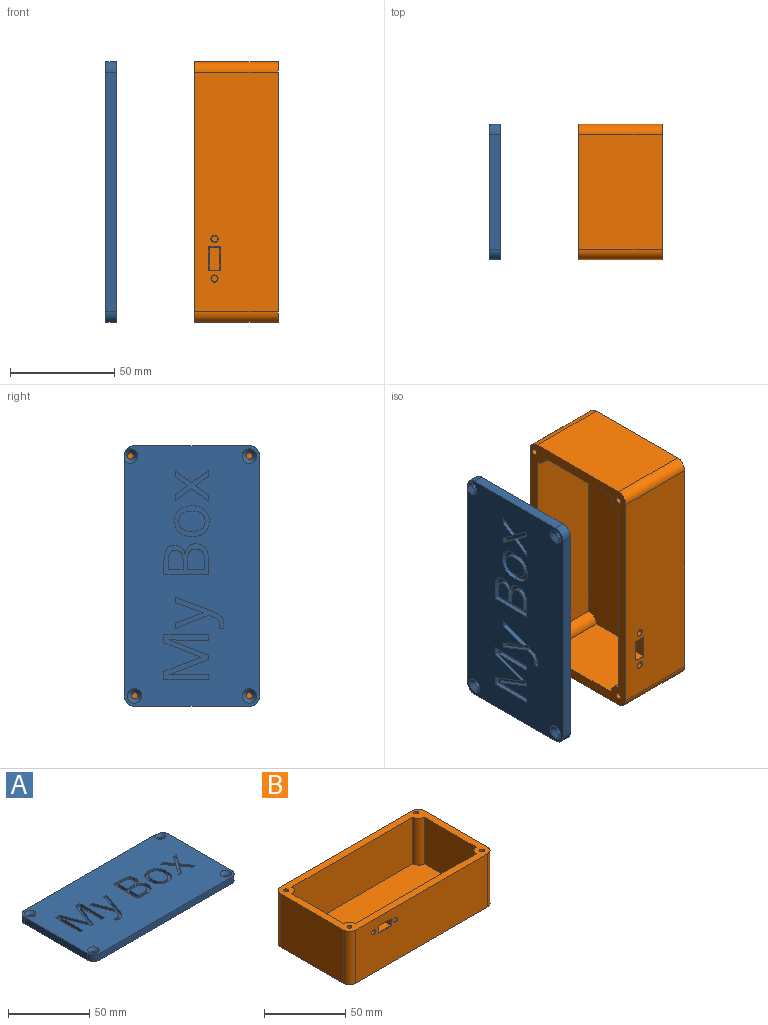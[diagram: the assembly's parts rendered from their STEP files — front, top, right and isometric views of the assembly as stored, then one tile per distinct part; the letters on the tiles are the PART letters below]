
ASSEMBLY  parts=2 mates=1
PART A: 114 faces, bbox 125.4x65.9x5.4 mm
  f0: plane 125x65mm, normal (0,0,1), area 7082mm2, adj f1,f2,f3,f4,f5,f6,f7,f12
  f1: plane 55x5mm, normal (1,0,0), area 275mm2, adj f0,f2,f12,f13
  f2: cylinder r=5mm len=5mm, axis (0,0,-1), area 38.5mm2, adj f0,f1,f3,f13,f112
  f3: plane 115.36x5.36mm, normal (0,1,0), area 574.4mm2, adj f0,f2,f4,f13,f112
  f4: cylinder r=5mm len=5mm, axis (0,0,-1), area 39.3mm2, adj f0,f3,f5,f13
  f5: plane 55x5mm, normal (-1,0,0), area 275mm2, adj f0,f4,f6,f13
  f6: cylinder r=5mm len=5mm, axis (0,0,-1), area 39.3mm2, adj f0,f5,f7,f13
  f7: plane 115x5mm, normal (0,-1,0), area 575mm2, adj f0,f6,f12,f13
  f8: cylinder r=1.5mm len=3mm, axis (0,0,-1), area 28.3mm2, adj f13,f110
  f9: cylinder r=1.5mm len=3mm, axis (0,0,-1), area 28.3mm2, adj f13,f112
  f10: cylinder r=1.5mm len=3mm, axis (0,0,-1), area 28.3mm2, adj f13,f113
  f11: cylinder r=1.5mm len=3mm, axis (0,0,-1), area 28.3mm2, adj f13,f111
  f12: cylinder r=5mm len=5mm, axis (0,0,-1), area 39.3mm2, adj f0,f1,f7,f13
  f13: plane 125x65mm, normal (0,0,-1), area 8075.3mm2, adj f1,f2,f3,f4,f5,f6,f7,f8
  f14: plane 2.62x2mm, normal (0,-1,0), area 5.2mm2, adj f0,f15,f29,f30
  f15: plane 16.2x6.5mm, normal (0.93,0.37,0), area 34.9mm2, adj f0,f14,f16,f30
  f16: plane 2.29x2mm, normal (0.93,-0.37,0), area 4.9mm2, adj f0,f15,f17,f30
  f17: extruded ~3.59x2.82mm, area 9.8mm2, adj f0,f16,f18,f30
  f18: extruded ~2x1.81mm, area 3.6mm2, adj f0,f17,f19,f30
  f19: plane 2x1.95mm, normal (1,0,0), area 3.9mm2, adj f0,f18,f20,f30
  f20: extruded ~2.21x2mm, area 4.5mm2, adj f0,f19,f21,f30
  f21: extruded ~3.37x2mm, area 7.3mm2, adj f0,f20,f22,f30
  f22: extruded ~3.86x2.4mm, area 9.2mm2, adj f0,f21,f23,f30
  f23: plane 18.35x6.93mm, normal (-0.94,0.35,0), area 39.2mm2, adj f0,f22,f24,f30
  f24: plane 2.62x2mm, normal (0,-1,0), area 5.2mm2, adj f0,f23,f25,f30
  f25: extruded ~11.16x3.99mm, area 23.7mm2, adj f0,f24,f26,f30
  f26: extruded ~2.57x2mm, area 5.4mm2, adj f0,f25,f27,f30
  f27: plane 2x0.12mm, normal (0,-1,0), area 0.2mm2, adj f0,f26,f28,f30
  f28: extruded ~4.54x2mm, area 9.5mm2, adj f0,f27,f29,f30
  f29: plane 9.19x3.53mm, normal (-0.93,-0.36,0), area 19.7mm2, adj f0,f14,f28,f30
  f30: plane 23.35x15.12mm, normal (0,0,1), area 100.8mm2, adj f14,f15,f16,f17,f18,f19,f20,f21
  f31: plane 7.87x5.6mm, normal (0.81,0.58,0), area 19.3mm2, adj f0,f32,f42,f43
  f32: plane 8.25x5.89mm, normal (0.81,-0.58,0), area 20.3mm2, adj f0,f31,f33,f43
  f33: plane 2.76x2mm, normal (0,1,0), area 5.5mm2, adj f0,f32,f34,f43
  f34: plane 6.53x4.56mm, normal (-0.82,0.57,0), area 15.9mm2, adj f0,f33,f35,f43
  f35: plane 6.53x4.52mm, normal (0.82,0.57,0), area 15.9mm2, adj f0,f34,f36,f43
  f36: plane 2.76x2mm, normal (0,1,0), area 5.5mm2, adj f0,f35,f37,f43
  f37: plane 8.25x5.89mm, normal (-0.81,-0.58,0), area 20.3mm2, adj f0,f36,f38,f43
  f38: plane 7.87x5.6mm, normal (-0.81,0.58,0), area 19.3mm2, adj f0,f37,f39,f43
  f39: plane 2.75x2mm, normal (0,-1,0), area 5.5mm2, adj f0,f38,f40,f43
  f40: plane 6.17x4.23mm, normal (0.82,-0.57,0), area 15mm2, adj f0,f39,f41,f43
  f41: plane 6.17x4.25mm, normal (-0.82,-0.57,0), area 15mm2, adj f0,f40,f42,f43
  f42: plane 2.78x2mm, normal (0,-1,0), area 5.6mm2, adj f0,f31,f41,f43
  f43: plane 16.11x14.6mm, normal (0,0,1), area 82.1mm2, adj f31,f32,f33,f34,f35,f36,f37,f38
  f44: extruded ~4.71x2mm, area 9.9mm2, adj f45,f60,f61,f108
  f45: extruded ~4.69x2mm, area 9.9mm2, adj f44,f46,f61,f108
  f46: extruded ~3.62x2mm, area 8.2mm2, adj f45,f47,f61,f108
  f47: extruded ~3.67x2mm, area 8.3mm2, adj f46,f48,f61,f108
  f48: extruded ~4.67x2mm, area 9.8mm2, adj f47,f49,f61,f108
  f49: extruded ~4.71x2mm, area 9.9mm2, adj f48,f50,f61,f108
  f50: extruded ~3.64x2mm, area 8.3mm2, adj f49,f60,f61,f108
  f51: extruded ~6.16x2mm, area 13.2mm2, adj f0,f52,f59,f61
  f52: extruded ~6.09x2mm, area 13.1mm2, adj f0,f51,f53,f61
  f53: extruded ~5.37x2.25mm, area 12mm2, adj f0,f52,f54,f61
  f54: extruded ~5.47x2.2mm, area 12.2mm2, adj f0,f53,f55,f61
  f55: extruded ~6.14x2mm, area 13.2mm2, adj f0,f54,f56,f61
  f56: extruded ~4.44x2mm, area 9.1mm2, adj f0,f55,f57,f61
  f57: extruded ~2.91x2.59mm, area 7.9mm2, adj f0,f56,f58,f61
  f58: extruded ~3.84x2mm, area 8mm2, adj f0,f57,f59,f61
  f59: extruded ~5.48x2.21mm, area 12.2mm2, adj f0,f51,f58,f61
  f60: extruded ~3.63x2mm, area 8.3mm2, adj f44,f50,f61,f108
  f61: plane 16.71x14.81mm, normal (0,0,1), area 99.7mm2, adj f44,f45,f46,f47,f48,f49,f50,f51
  f62: plane 8.04x2mm, normal (-1,0,0), area 16.1mm2, adj f63,f86,f87,f109
  f63: plane 4.28x2mm, normal (0,1,0), area 8.6mm2, adj f62,f64,f87,f109
  f64: extruded ~4.09x2mm, area 8.5mm2, adj f63,f65,f87,f109
  f65: extruded ~2.94x2mm, area 6.7mm2, adj f64,f66,f87,f109
  f66: extruded ~3.16x2mm, area 7.1mm2, adj f65,f67,f87,f109
  f67: extruded ~3.92x2mm, area 8.2mm2, adj f66,f86,f87,f109
  f68: plane 4.12x2mm, normal (0,-1,0), area 8.2mm2, adj f69,f84,f87,f88
  f69: plane 7.04x2mm, normal (-1,0,0), area 14.1mm2, adj f68,f70,f87,f88
  f70: plane 3.68x2mm, normal (0,1,0), area 7.4mm2, adj f69,f71,f87,f88
  f71: extruded ~4.12x2mm, area 8.5mm2, adj f70,f72,f87,f88
  f72: extruded ~2.61x2mm, area 6.1mm2, adj f71,f73,f87,f88
  f73: extruded ~2.8x2mm, area 6.3mm2, adj f72,f84,f87,f88
  f74: plane 6.07x2mm, normal (0,-1,0), area 12.1mm2, adj f0,f75,f85,f87
  f75: plane 21.5x2mm, normal (1,0,0), area 43mm2, adj f0,f74,f76,f87
  f76: plane 7.5x2mm, normal (0,1,0), area 15mm2, adj f0,f75,f77,f87
  f77: extruded ~5.45x2mm, area 11.6mm2, adj f0,f76,f78,f87
  f78: extruded ~4.5x2mm, area 10.1mm2, adj f0,f77,f79,f87
  f79: extruded ~5.15x4.9mm, area 15.7mm2, adj f0,f78,f80,f87
  f80: plane 2x0.15mm, normal (-1,0,0), area 0.3mm2, adj f0,f79,f81,f87
  f81: extruded ~3.11x2mm, area 7.1mm2, adj f0,f80,f82,f87
  f82: extruded ~3.16x2mm, area 6.8mm2, adj f0,f81,f83,f87
  f83: extruded ~4.04x2mm, area 9.3mm2, adj f0,f82,f85,f87
  f84: extruded ~3.81x2mm, area 7.9mm2, adj f68,f73,f87,f88
  f85: extruded ~6.19x2mm, area 12.8mm2, adj f0,f74,f83,f87
  f86: plane 4.49x2mm, normal (0,-1,0), area 9mm2, adj f62,f67,f87,f109
  f87: plane 21.5x14.89mm, normal (0,0,1), area 157.6mm2, adj f62,f63,f64,f65,f66,f67,f68,f69
  f88: plane 9.09x7.04mm, normal (0,0,1), area 58.5mm2, adj f68,f69,f70,f71,f72,f73,f84
  f89: plane 19.05x7.29mm, normal (0.93,0.36,0), area 40.8mm2, adj f0,f90,f106,f107
  f90: plane 2.01x2mm, normal (0,1,0), area 4mm2, adj f0,f89,f91,f107
  f91: plane 19.03x7.35mm, normal (-0.93,0.36,0), area 40.8mm2, adj f0,f90,f92,f107
  f92: plane 2x0.12mm, normal (0,1,0), area 0.2mm2, adj f0,f91,f93,f107
  f93: extruded ~5.18x2mm, area 10.4mm2, adj f0,f92,f94,f107
  f94: plane 13.85x2mm, normal (1,0,0), area 27.7mm2, adj f0,f93,f95,f107
  f95: plane 2.5x2mm, normal (0,1,0), area 5mm2, adj f0,f94,f96,f107
  f96: plane 21.5x2mm, normal (-1,0,0), area 43mm2, adj f0,f95,f97,f107
  f97: plane 3.74x2mm, normal (0,-1,0), area 7.5mm2, adj f0,f96,f98,f107
  f98: plane 17.73x6.86mm, normal (0.93,-0.36,0), area 38mm2, adj f0,f97,f99,f107
  f99: plane 2x0.12mm, normal (0,-1,0), area 0.2mm2, adj f0,f98,f100,f107
  f100: plane 17.73x6.81mm, normal (-0.93,-0.36,0), area 38mm2, adj f0,f99,f101,f107
  f101: plane 3.76x2mm, normal (0,-1,0), area 7.5mm2, adj f0,f100,f102,f107
  f102: plane 21.5x2mm, normal (1,0,0), area 43mm2, adj f0,f101,f103,f107
  f103: plane 2.31x2mm, normal (0,1,0), area 4.6mm2, adj f0,f102,f104,f107
  f104: plane 13.67x2mm, normal (-1,0,0), area 27.3mm2, adj f0,f103,f105,f107
  f105: extruded ~5.38x2mm, area 10.8mm2, adj f0,f104,f106,f107
  f106: plane 2x0.12mm, normal (0,1,0), area 0.2mm2, adj f0,f89,f105,f107
  f107: plane 21.5x21.29mm, normal (0,0,1), area 197.6mm2, adj f89,f90,f91,f92,f93,f94,f95,f96
  f108: plane 12.58x9.75mm, normal (0,0,1), area 101.8mm2, adj f44,f45,f46,f47,f48,f49,f50,f60
  f109: plane 9.72x8.04mm, normal (0,0,1), area 71.2mm2, adj f62,f63,f64,f65,f66,f67,f86
  f110: cone r=1.5mm half-angle=45deg, axis (0,0,1), area 44.4mm2, adj f0,f8
  f111: cone r=1.5mm half-angle=45deg, axis (0,0,1), area 44.4mm2, adj f0,f11
  f112: cone r=1.5mm half-angle=45deg, axis (0,0,1), area 42.7mm2, adj f0,f2,f3,f9
  f113: cone r=1.5mm half-angle=45deg, axis (0,0,1), area 44.4mm2, adj f0,f10
PART B: 39 faces, bbox 125x65x40 mm
  f0: plane 115x55mm, normal (0,0,1), area 6246.5mm2, adj f1,f2,f3,f4,f19,f20,f21,f22
  f1: plane 45x35mm, normal (-1,0,0), area 1575mm2, adj f0,f10,f20,f21
  f2: plane 105x35mm, normal (0,-1,0), area 3675mm2, adj f0,f10,f21,f22
  f3: plane 45x35mm, normal (1,0,0), area 1575mm2, adj f0,f10,f19,f22
  f4: plane 105x35mm, normal (0,1,0), area 3605.9mm2, adj f0,f10,f19,f20,f27,f28,f29,f30
  f5: plane 55x40mm, normal (1,0,0), area 2200mm2, adj f9,f10,f23,f26
  f6: plane 115x40mm, normal (0,1,0), area 4600mm2, adj f9,f10,f23,f24
  f7: plane 55x40mm, normal (-1,0,0), area 2200mm2, adj f9,f10,f24,f25
  f8: plane 115x40mm, normal (0,-1,0), area 4520.3mm2, adj f9,f10,f25,f26,f33,f34,f35,f36
  f9: plane 125x65mm, normal (0,0,-1), area 8103.5mm2, adj f5,f6,f7,f8,f23,f24,f25,f26
  f10: plane 125x65mm, normal (0,0,1), area 1828.8mm2, adj f1,f2,f3,f4,f5,f6,f7,f8
  f11: cylinder r=1.5mm len=15mm, axis (0,0,1), area 141.4mm2, adj f10,f12
  f12: plane 3x3mm, normal (0,0,1), area 7.1mm2, adj f11
  f13: cylinder r=1.5mm len=15mm, axis (0,0,1), area 141.4mm2, adj f10,f14
  f14: plane 3x3mm, normal (0,0,1), area 7.1mm2, adj f13
  f15: cylinder r=1.5mm len=15mm, axis (0,0,1), area 141.4mm2, adj f10,f16
  f16: plane 3x3mm, normal (0,0,1), area 7.1mm2, adj f15
  f17: cylinder r=1.5mm len=15mm, axis (0,0,1), area 141.4mm2, adj f10,f18
  f18: plane 3x3mm, normal (0,0,1), area 7.1mm2, adj f17
  f19: cylinder r=5mm len=35mm, axis (0,0,1), area 274.9mm2, adj f0,f3,f4,f10
  f20: cylinder r=5mm len=35mm, axis (0,0,1), area 274.9mm2, adj f0,f1,f4,f10
  f21: cylinder r=5mm len=35mm, axis (0,0,1), area 274.9mm2, adj f0,f1,f2,f10
  f22: cylinder r=5mm len=35mm, axis (0,0,1), area 274.9mm2, adj f0,f2,f3,f10
  f23: cylinder r=5mm len=40mm, axis (0,0,1), area 314.2mm2, adj f5,f6,f9,f10
  f24: cylinder r=5mm len=40mm, axis (0,0,-1), area 314.2mm2, adj f6,f7,f9,f10
  f25: cylinder r=5mm len=40mm, axis (0,0,1), area 314.2mm2, adj f7,f8,f9,f10
  f26: cylinder r=5mm len=40mm, axis (0,0,-1), area 314.2mm2, adj f5,f8,f9,f10
  f27: plane 11x4.8mm, normal (0,0,1), area 52.8mm2, adj f4,f28,f29,f34
  f28: plane 5x4.8mm, normal (1,0,0), area 24mm2, adj f4,f27,f30,f33
  f29: plane 5x4.8mm, normal (-1,0,0), area 24mm2, adj f4,f27,f30,f36
  f30: plane 11x4.8mm, normal (0,0,-1), area 52.8mm2, adj f4,f28,f29,f35
  f31: cylinder r=1.5mm len=4.8mm, axis (0,-1,0), area 45.2mm2, adj f4,f38
  f32: cylinder r=1.5mm len=4.8mm, axis (0,-1,0), area 45.2mm2, adj f4,f37
  f33: plane 5.4x0.2mm, normal (0.71,-0.71,0), area 1.5mm2, adj f8,f28,f34,f35
  f34: plane 11.4x0.2mm, normal (0,-0.71,0.71), area 3.2mm2, adj f8,f27,f33,f36
  f35: plane 11.4x0.2mm, normal (0,-0.71,-0.71), area 3.2mm2, adj f8,f30,f33,f36
  f36: plane 5.4x0.2mm, normal (-0.71,-0.71,0), area 1.5mm2, adj f8,f29,f34,f35
  f37: cone r=1.5mm half-angle=45deg, axis (0,-1,0), area 2.8mm2, adj f8,f32
  f38: cone r=1.5mm half-angle=45deg, axis (0,-1,0), area 2.8mm2, adj f8,f31
PLACE A rot(axis=(0,-1,0),90deg) t=(-37.61,0,62.5)mm
PLACE B rot(axis=(0,-1,0),90deg) t=(0,0,62.5)mm
MATE slider A.f13 <-> B.f10  axis (-1,0,0) through (-77.61,-32.5,5)mm
